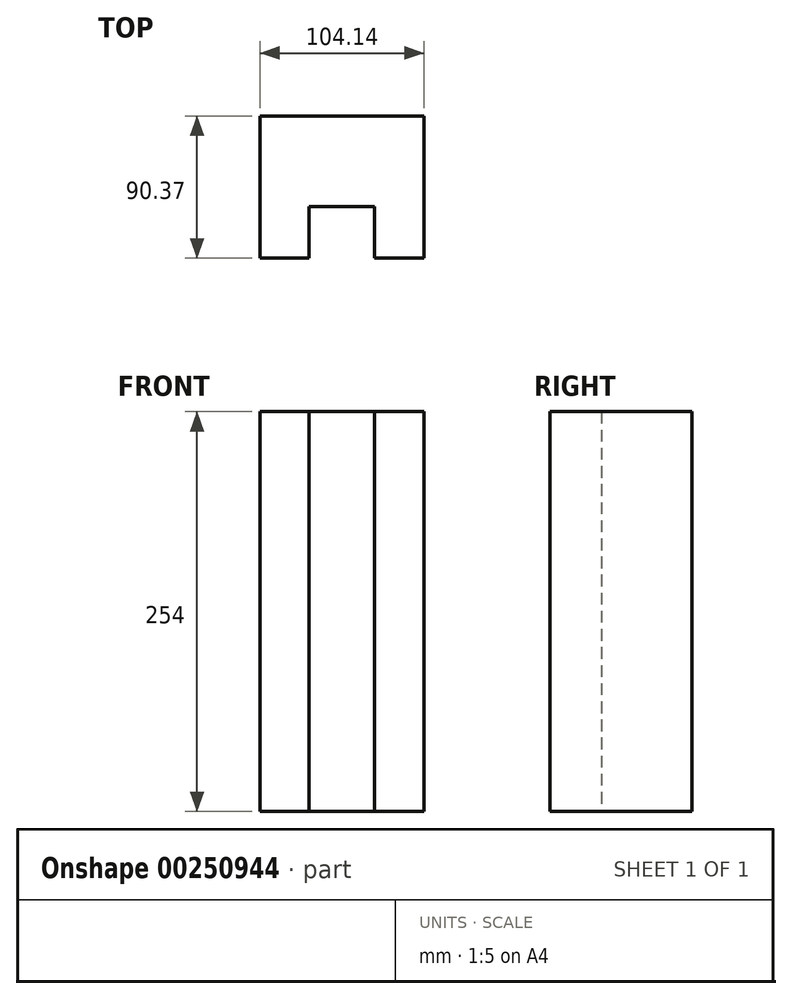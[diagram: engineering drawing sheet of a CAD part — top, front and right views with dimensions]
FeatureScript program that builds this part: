
annotation { "Feature Type Name" : "Feature", "Feature Type Description" : "" }
export const myFeature = defineFeature(function(context is Context, id is Id, definition is map)
    precondition{}
    {
        {
            var Q0;
            Q0=qCreatedBy(makeId("Top.planeOp"),FACE);
            var sketch = newSketch(context, id + "F0", { "sketchPlane" : qUnion([Q0])});
            skLineSegment(sketch, "E0", {"start": v(-55.08, 39.16) * mm, "end": v(-55.08, -51.2) * mm});
            skLineSegment(sketch, "E1", {"start": v(-55.08, -51.2) * mm, "end": v(-23.81, -51.2) * mm});
            skLineSegment(sketch, "E2", {"start": v(-23.81, -51.2) * mm, "end": v(-23.81, -18.5) * mm});
            skLineSegment(sketch, "E3", {"start": v(-23.81, -18.5) * mm, "end": v(17.79, -18.5) * mm});
            skLineSegment(sketch, "E4", {"start": v(17.79, -18.5) * mm, "end": v(17.79, -51.2) * mm});
            skLineSegment(sketch, "E5", {"start": v(17.79, -51.2) * mm, "end": v(49.06, -51.2) * mm});
            skLineSegment(sketch, "E6", {"start": v(49.06, -51.2) * mm, "end": v(49.06, 40.02) * mm});
            skLineSegment(sketch, "E7", {"start": v(-55.08, 39.16) * mm, "end": v(49.06, 39.16) * mm});
            skPoint(sketch, "E8", {"position": v(0, 0) * mm});
            skSolve(sketch);
        }
        {
            var Q0;
            Q0=makeQuery(id+"F0.imprint","IMPRINT",FACE,{"disambiguationData":[TD([[makeQuery(id+"F0.imprint","IMPRINT",EDGE,{"derivedFrom":sQuery(id+"F0.wireOp",EDGE,"E0")}),1.0]])]});
            extrude(context, id + "F1", {"entities" : qUnion([Q0]), "depth" : 254 * mm});
        }
    });
